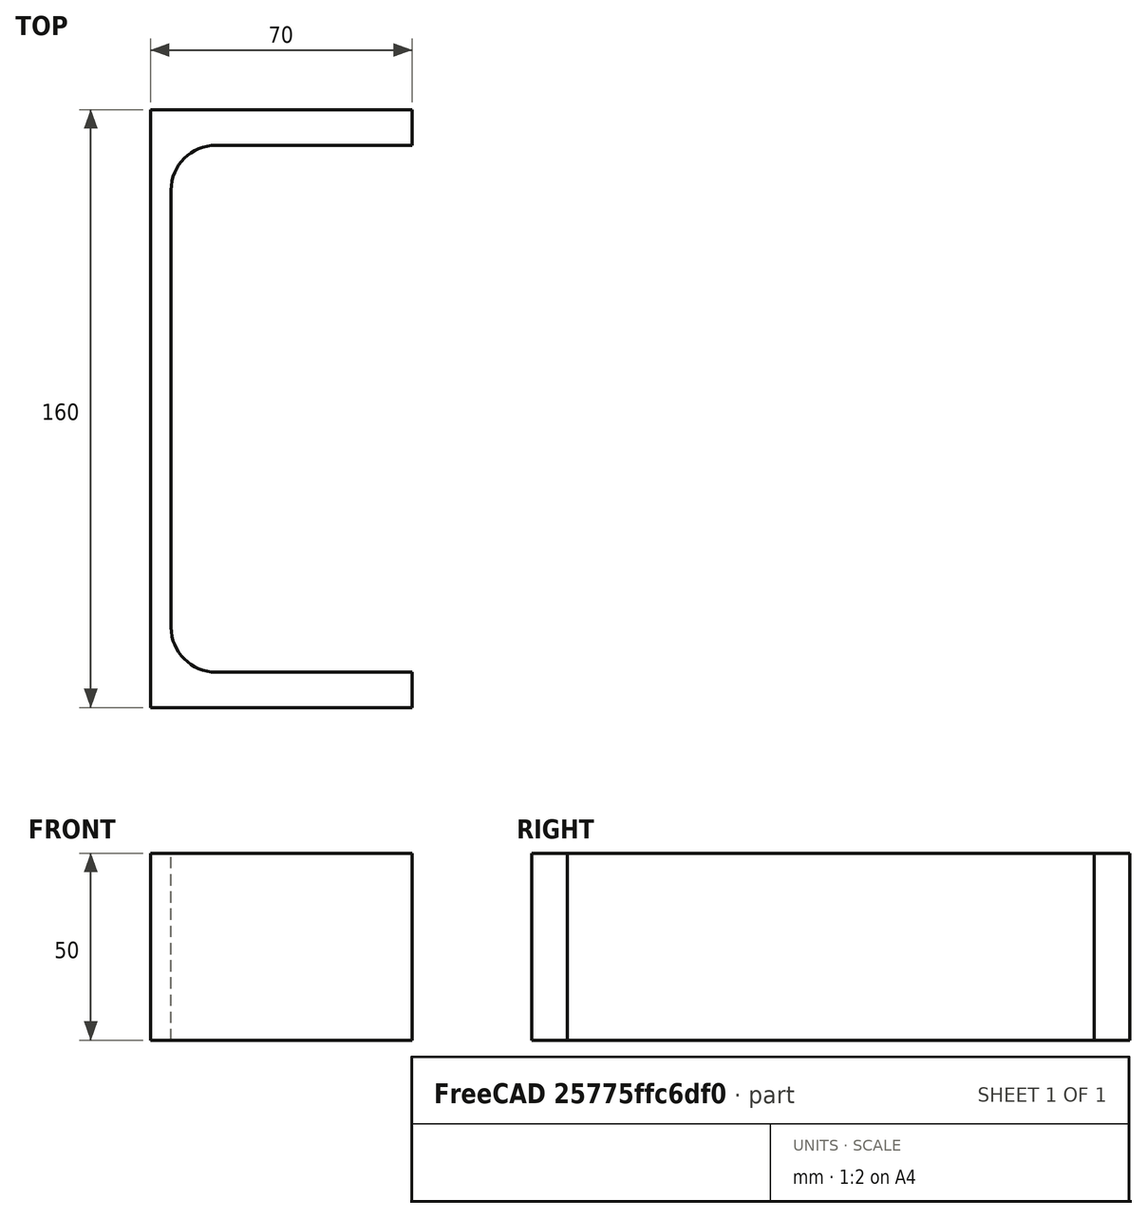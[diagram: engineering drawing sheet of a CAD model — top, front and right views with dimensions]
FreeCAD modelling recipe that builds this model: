
FCSTD DOCUMENT  (FreeCAD 0.20R29410 (Git))
Label: UPE-Profile 160 DIN1026-2 S235JR
License: All rights reserved
LicenseURL: http://en.wikipedia.org/wiki/All_rights_reserved
objects: Sketcher::SketchObject×1, Part::Extrusion×1
note: 2 computed .brp shape members not serialized (recipe doc carries the construction recipe); baked Part::Feature solids carry a one-line shape summary decoded from their .brp

FEATURE [Sketcher::SketchObject] Sketch
  FullyConstrained = true
  MapMode = 5
  sketch-geometry (10):
    g0: LineSegment StartX=5.5 StartY=-58.5 StartZ=0 EndX=5.5 EndY=58.5 EndZ=0
    g1: LineSegment StartX=17.5 StartY=70.5 StartZ=0 EndX=70 EndY=70.5 EndZ=0
    g2: LineSegment StartX=70 StartY=70.5 StartZ=0 EndX=70 EndY=80 EndZ=0
    g3: LineSegment StartX=70 StartY=-80 StartZ=0 EndX=70 EndY=-70.5 EndZ=0
    g4: LineSegment StartX=70 StartY=-70.5 StartZ=0 EndX=17.5 EndY=-70.5 EndZ=0
    g5: ArcOfCircle CenterX=17.5 CenterY=58.5 CenterZ=0 NormalX=0 NormalY=0 NormalZ=1 AngleXU=0 Radius=12 StartAngle=1.5708 EndAngle=3.14159
    g6: ArcOfCircle CenterX=17.5 CenterY=-58.5 CenterZ=0 NormalX=0 NormalY=0 NormalZ=1 AngleXU=0 Radius=12 StartAngle=3.14159 EndAngle=4.71239
    g7: LineSegment StartX=70 StartY=-80 StartZ=0 EndX=0 EndY=-80 EndZ=0
    g8: LineSegment StartX=0 StartY=-80 StartZ=0 EndX=0 EndY=80 EndZ=0
    g9: LineSegment StartX=0 StartY=80 StartZ=0 EndX=70 EndY=80 EndZ=0
  constraints (27):
    c: Vertical(g0)
    c: Coincident(g2,g1)
    c: Vertical(g2)
    c: Vertical(g3)
    c: Coincident(g4,g3)
    c: Horizontal(g4)
    c: Tangent(g1,g5) = 1.5708
    c: Tangent(g0,g5) = 1.5708
    c: Tangent(g0,g6) = 1.5708
    c: Tangent(g4,g6) = 1.5708
    c: Symmetric(g2,g3,g-1)
    c: DistanceY(g2) = 9.5
    c: Radius(g5) = 12
    c: Coincident(g3,g7)
    c: PointOnObject(g7,g-2)
    c: Horizontal(g7)
    c: Coincident(g7,g8)
    c: PointOnObject(g8,g-2)
    c: Coincident(g8,g9)
    c: Coincident(g9,g2)
    c: Horizontal(g9)
    c: Distance(g-1,g0) = 5.5
    c: DistanceX(g9,g9) = 70
    c: Horizontal(g1)
    c: Equal(g3,g2)
    c: Equal(g5,g6)
    c: DistanceY(g3,g2) = 160
FEATURE [Part::Extrusion] Extrude  label="UPE-Profile 160 DIN1026-2 S235JR"
  Base = -> Sketch
  Dir = (0,0,50)
  DirMode = 0
  FaceMakerClass = Part::FaceMakerExtrusion
  LengthFwd = 0
  LengthRev = 0
  Solid = true
  Symmetric = false
